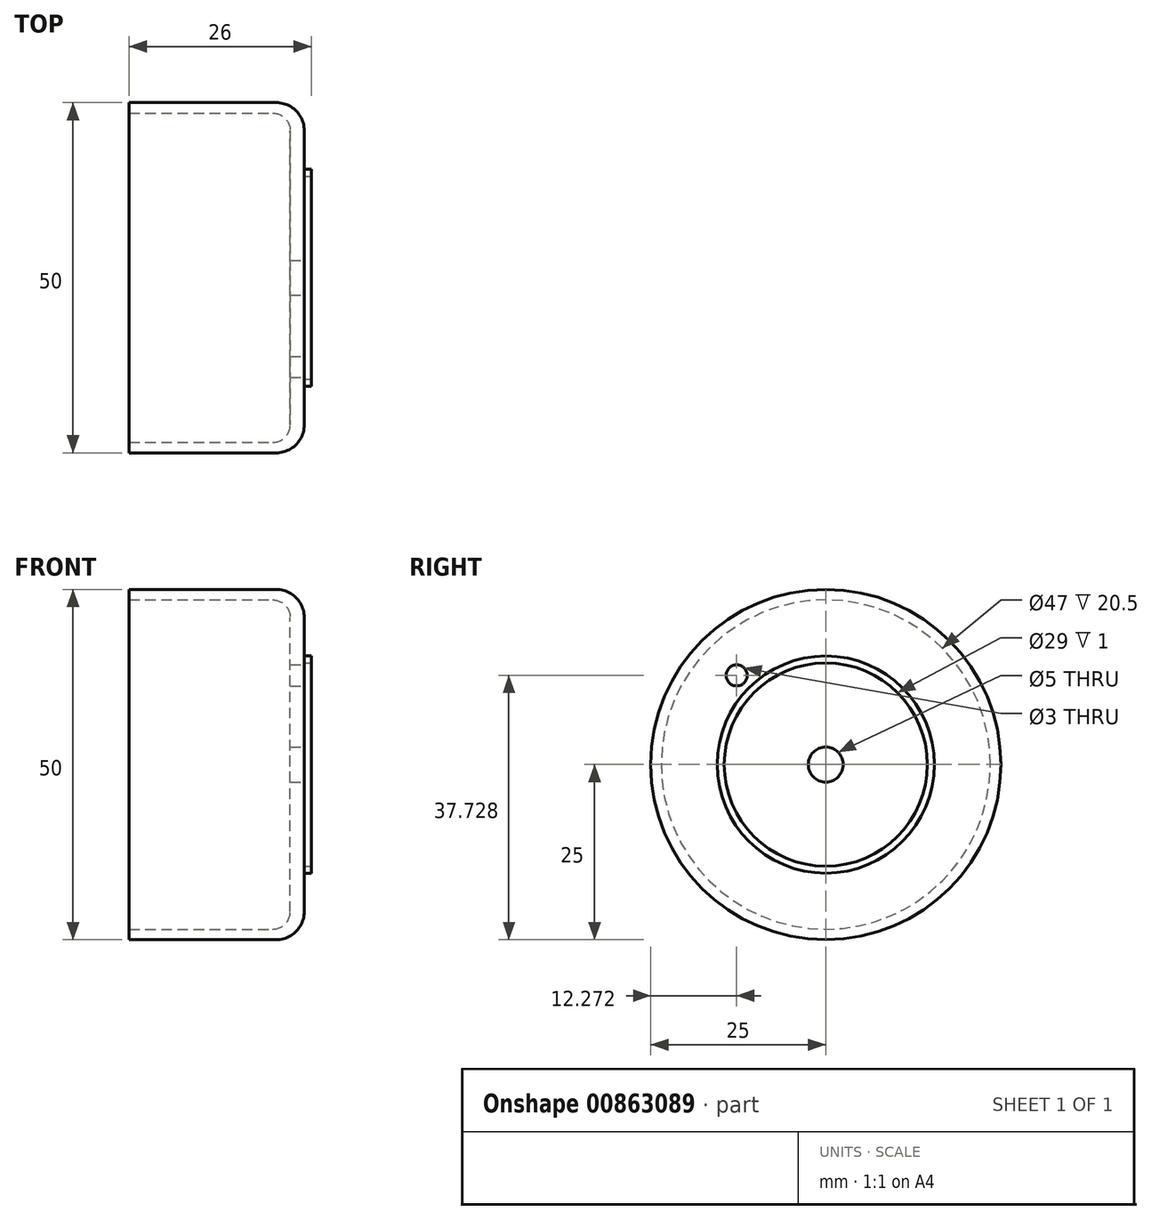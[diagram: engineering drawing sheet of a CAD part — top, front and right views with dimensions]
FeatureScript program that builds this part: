
annotation { "Feature Type Name" : "Feature", "Feature Type Description" : "" }
export const myFeature = defineFeature(function(context is Context, id is Id, definition is map)
    precondition{}
    {
        {
            var Q0;
            Q0=qCreatedBy(makeId("Front.planeOp"),FACE);
            var sketch = newSketch(context, id + "F0", { "sketchPlane" : qUnion([Q0])});
            skLineSegment(sketch, "E0", {"start": v(0, 23.5) * mm, "end": v(0, 25) * mm});
            skLineSegment(sketch, "E1", {"start": v(0, 25) * mm, "end": v(21, 25) * mm});
            skLineSegment(sketch, "E2", {"start": v(25, 21) * mm, "end": v(25, 15.5) * mm});
            skLineSegment(sketch, "E3", {"start": v(25, 0) * mm, "end": v(23, 0) * mm});
            skLineSegment(sketch, "E4", {"start": v(23, 0) * mm, "end": v(23, 21) * mm});
            skLineSegment(sketch, "E5", {"start": v(20.5, 23.5) * mm, "end": v(0, 23.5) * mm});
            skPoint(sketch, "E6.visualSharp", {"position": v(23, 23.5) * mm});
            skArc(sketch, "E6.filletArc", {"start": v(23, 21) * mm, "mid": v(22.27, 22.77) * mm, "end": v(20.5, 23.5) * mm});
            skPoint(sketch, "E7.visualSharp", {"position": v(25, 25) * mm});
            skArc(sketch, "E7.filletArc", {"start": v(25, 21) * mm, "mid": v(23.83, 23.83) * mm, "end": v(21, 25) * mm});
            skLineSegment(sketch, "E8", {"start": v(25, 15.5) * mm, "end": v(26, 15.5) * mm});
            skLineSegment(sketch, "E9", {"start": v(26, 15.5) * mm, "end": v(26, 14.5) * mm});
            skLineSegment(sketch, "E10", {"start": v(26, 14.5) * mm, "end": v(25, 14.5) * mm});
            skLineSegment(sketch, "E11.trimOffspring", {"start": v(25, 14.5) * mm, "end": v(25, 0) * mm});
            skSolve(sketch);
        }
        {
            var Q0;
            Q0=makeQuery(id+"F0.imprint","IMPRINT",FACE,{"disambiguationData":[TD([[makeQuery(id+"F0.imprint","IMPRINT",EDGE,{"derivedFrom":sQuery(id+"F0.wireOp",EDGE,"E0")}),-1.0]])]});
            var Q1;
            Q1=sQuery(id+"F0.wireOp",EDGE,"E3");
            revolve(context, id + "F1", {"surfaceOperationType" : NewSurfaceOperationType.NEW, "entities" : qUnion([Q0]), "axis" : qUnion([Q1]), "revolveType" : RevolveType.FULL});
        }
        {
            var Q0;
            Q0=makeQuery(id+"F1.opRevolve","SWEPT_FACE",FACE,{"disambiguationData":[OSD([sQuery(id+"F0.wireOp",EDGE,"E11.trimOffspring")])]});
            var sketch = newSketch(context, id + "F2", { "sketchPlane" : qUnion([Q0])});
            skCircle(sketch, "E12", {"center": v(0, 0) * mm, "radius": 2.5 * mm});
            skLineSegment(sketch, "E13", {"start": v(0, 0) * mm, "end": v(-12.73, 12.73) * mm, "construction": true});
            skCircle(sketch, "E14", {"center": v(-12.73, 12.73) * mm, "radius": 1.5 * mm});
            skSolve(sketch);
        }
        {
            var Q0;
            Q0=makeQuery(id+"F2.imprint","IMPRINT",FACE,{"disambiguationData":[TD([[makeQuery(id+"F2.imprint","IMPRINT",EDGE,{"derivedFrom":sQuery(id+"F2.wireOp",EDGE,"E12")}),1.0]])]});
            extrude(context, id + "F3", {"entities" : qUnion([Q0]), "operationType" : NewBodyOperationType.REMOVE, "endBound" : BoundingType.THROUGH_ALL, "oppositeDirection" : true, "depth" : 25 * mm, "offsetDistance" : 25 * mm});
        }
        {
            var Q0;
            Q0=makeQuery(id+"F2.imprint","IMPRINT",FACE,{"disambiguationData":[TD([[makeQuery(id+"F2.imprint","IMPRINT",EDGE,{"derivedFrom":sQuery(id+"F2.wireOp",EDGE,"E14")}),1.0]])]});
            extrude(context, id + "F4", {"entities" : qUnion([Q0]), "operationType" : NewBodyOperationType.REMOVE, "endBound" : BoundingType.THROUGH_ALL, "oppositeDirection" : true, "depth" : 25 * mm, "offsetDistance" : 25 * mm});
        }
    });
